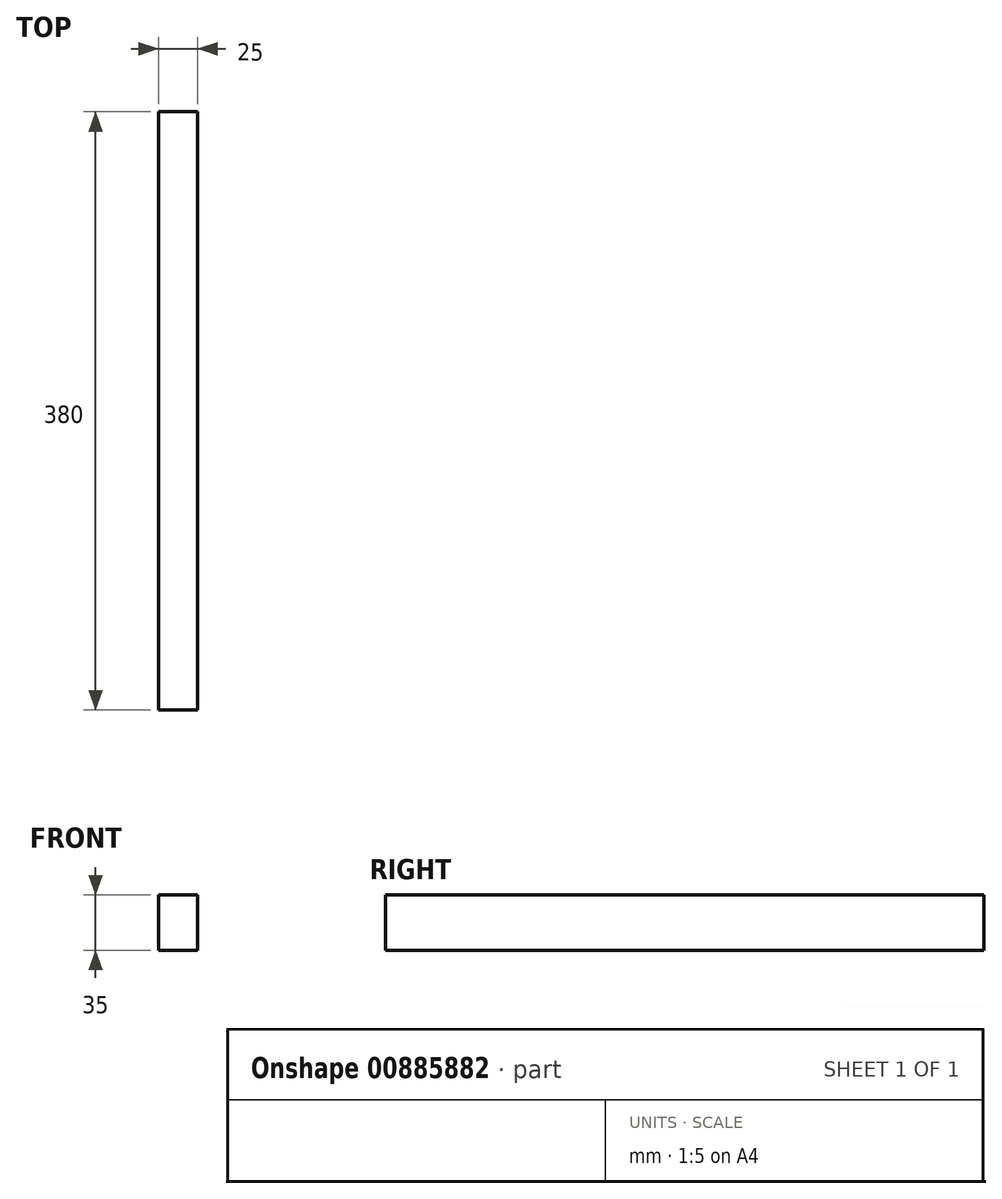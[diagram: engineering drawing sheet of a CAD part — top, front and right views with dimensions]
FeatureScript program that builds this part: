
annotation { "Feature Type Name" : "Feature", "Feature Type Description" : "" }
export const myFeature = defineFeature(function(context is Context, id is Id, definition is map)
    precondition{}
    {
        {
            var Q0;
            Q0=qCreatedBy(makeId("Front.planeOp"),FACE);
            var sketch = newSketch(context, id + "F0", { "sketchPlane" : qUnion([Q0])});
            skLineSegment(sketch, "E0.bottom", {"start": v(12.5, 17.5) * mm, "end": v(-12.5, 17.5) * mm});
            skLineSegment(sketch, "E0.top", {"start": v(12.5, -17.5) * mm, "end": v(-12.5, -17.5) * mm});
            skLineSegment(sketch, "E0.left", {"start": v(12.5, 17.5) * mm, "end": v(12.5, -17.5) * mm});
            skLineSegment(sketch, "E0.right", {"start": v(-12.5, 17.5) * mm, "end": v(-12.5, -17.5) * mm});
            skPoint(sketch, "E0.middle", {"position": v(0, 0) * mm});
            skSolve(sketch);
        }
        {
            var Q0;
            Q0 = qSketchRegion(id + "F0", true);
            extrude(context, id + "F1", {"entities" : qUnion([Q0]), "oppositeDirection" : true, "depth" : 380 * mm, "offsetDistance" : 25 * mm});
        }
    });
